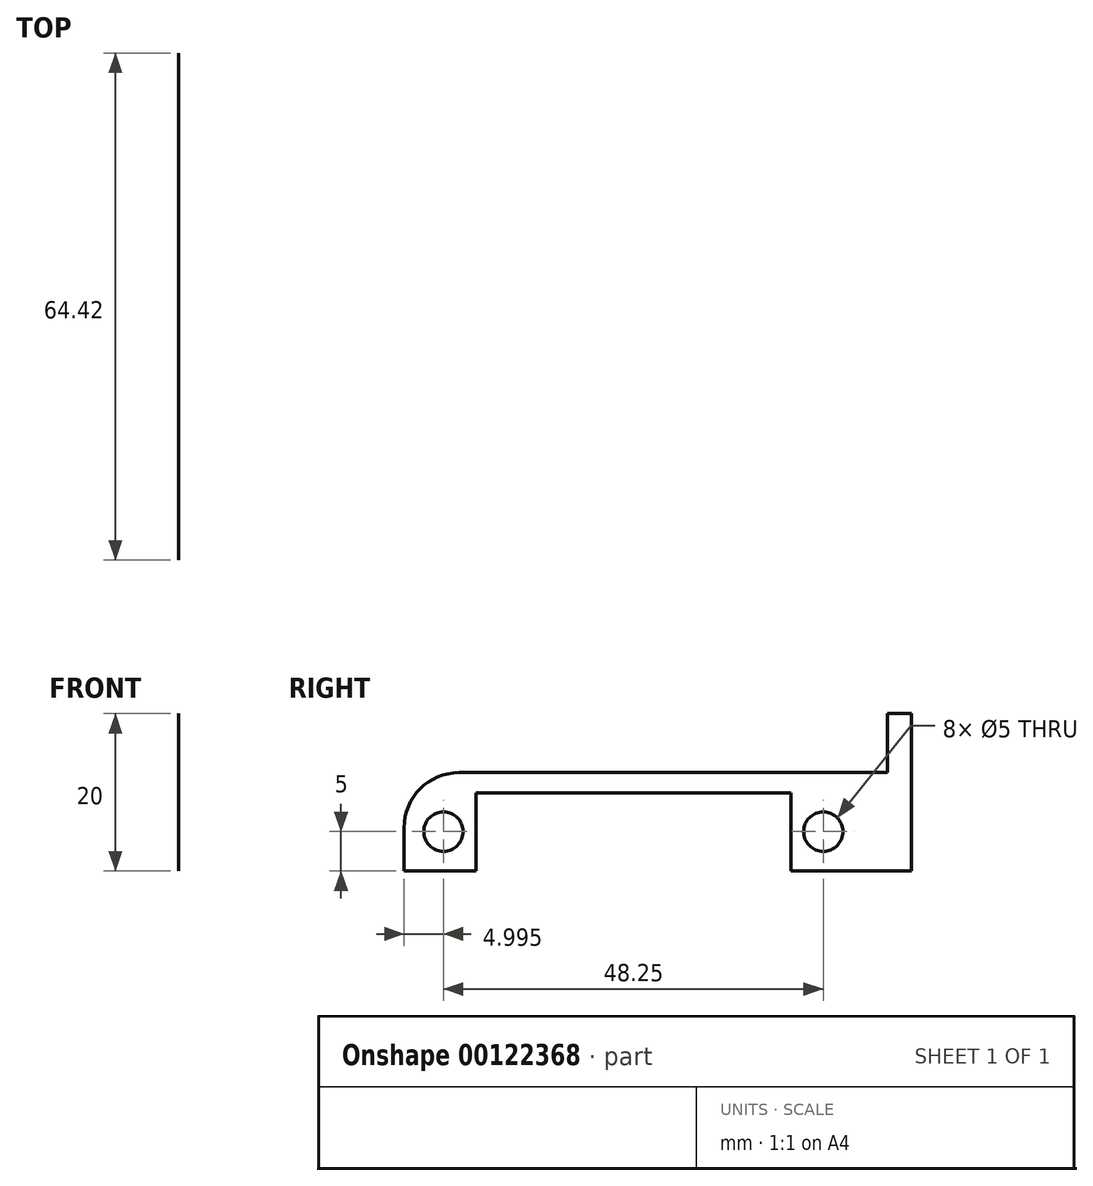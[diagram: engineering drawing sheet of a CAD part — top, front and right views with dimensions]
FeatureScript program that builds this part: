
annotation { "Feature Type Name" : "Feature", "Feature Type Description" : "" }
export const myFeature = defineFeature(function(context is Context, id is Id, definition is map)
    precondition{}
    {
        {
            var Q0;
            Q0=qCreatedBy(makeId("Right.planeOp"),FACE);
            var sketch = newSketch(context, id + "F0", { "sketchPlane" : qUnion([Q0])});
            skLineSegment(sketch, "E0.bottom", {"start": v(0, 0) * mm, "end": v(40, 0) * mm});
            skLineSegment(sketch, "E0.top", {"start": v(0, 9.9) * mm, "end": v(40, 9.9) * mm});
            skLineSegment(sketch, "E0.left", {"start": v(0, 0) * mm, "end": v(0, 9.9) * mm});
            skLineSegment(sketch, "E0.right", {"start": v(40, 0) * mm, "end": v(40, 9.9) * mm});
            skCircle(sketch, "E1", {"center": v(44.12, 5) * mm, "radius": 2.5 * mm});
            skLineSegment(sketch, "E2", {"start": v(20, 0) * mm, "end": v(20, 9.9) * mm});
            skCircle(sketch, "E3", {"center": v(-4.12, 5) * mm, "radius": 2.5 * mm});
            skLineSegment(sketch, "E4.bottom", {"start": v(-9.13, 12.5) * mm, "end": v(52.3, 12.5) * mm});
            skLineSegment(sketch, "E4.top", {"start": v(-9.13, 0) * mm, "end": v(52.3, 0) * mm});
            skLineSegment(sketch, "E4.left", {"start": v(-9.12, 12.5) * mm, "end": v(-9.12, 0) * mm});
            skLineSegment(sketch, "E5.bottom", {"start": v(52.3, 0) * mm, "end": v(55.3, 0) * mm});
            skLineSegment(sketch, "E5.top", {"start": v(52.3, 20) * mm, "end": v(55.3, 20) * mm});
            skLineSegment(sketch, "E5.left", {"start": v(52.3, 12.5) * mm, "end": v(52.3, 20) * mm});
            skLineSegment(sketch, "E5.right", {"start": v(55.3, 0) * mm, "end": v(55.3, 20) * mm});
            skSolve(sketch);
        }
        {
            var Q0;
            {var subQ4=sQuery(id+"F0.wireOp",EDGE,"E0.left");Q0=makeQuery(id+"F0.imprint","IMPRINT",FACE,{"disambiguationData":[TD([[makeQuery(id+"F0.imprint","IMPRINT",EDGE,{"derivedFrom":subQ4}),1.0]])]});}
            extrude(context, id + "F1", {"entities" : qUnion([Q0]), "depth" : 1 / 203.2 * mm});
        }
        {
            var Q0;
            Q0=makeQuery(id+"F1.opExtrude","SWEPT_EDGE",EDGE,{"disambiguationData":[OSD([sQuery(id+"F0.wireOp",EDGE,"E4.bottom"),sQuery(id+"F0.wireOp",EDGE,"E4.left")])]});
            fillet(context, id + "F2", {"entities" : qUnion([Q0]), "radius" : 7 * mm, "tangentPropagation" : true, "allowEdgeOverflow" : false});
        }
    });
